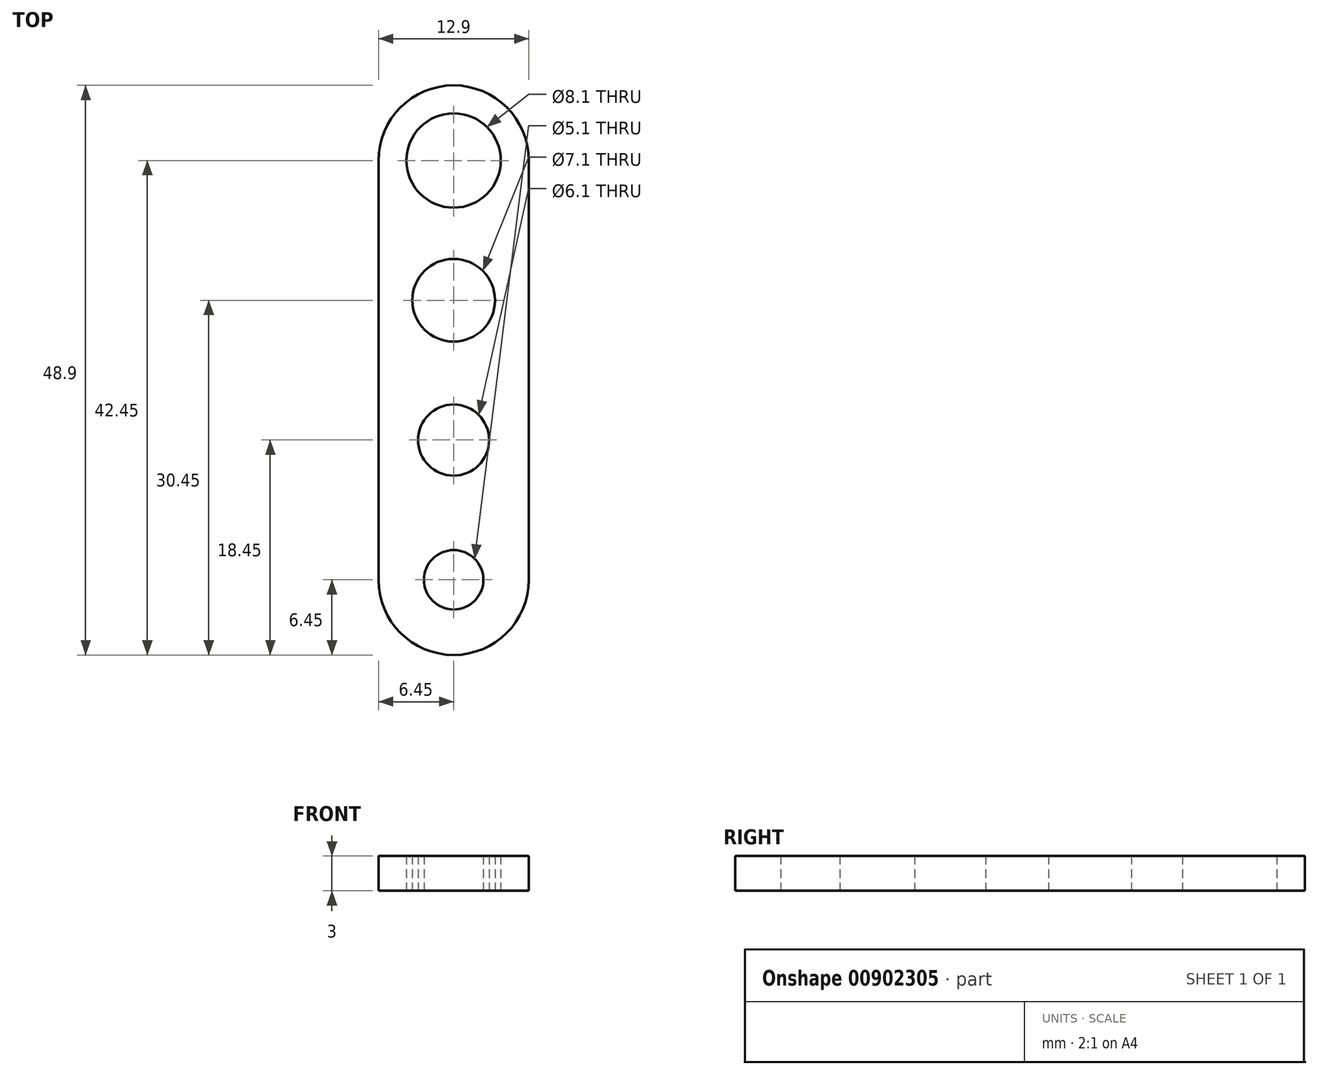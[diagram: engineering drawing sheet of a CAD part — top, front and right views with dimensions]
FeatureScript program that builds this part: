
annotation { "Feature Type Name" : "Feature", "Feature Type Description" : "" }
export const myFeature = defineFeature(function(context is Context, id is Id, definition is map)
    precondition{}
    {
        {
            var Q0;
            Q0=qCreatedBy(makeId("Top.planeOp"),FACE);
            var sketch = newSketch(context, id + "F0", { "sketchPlane" : qUnion([Q0])});
            skLineSegment(sketch, "E0.left", {"start": v(-6.45, -18) * mm, "end": v(-6.45, 18) * mm});
            skLineSegment(sketch, "E0.right", {"start": v(6.45, -18) * mm, "end": v(6.45, 18) * mm});
            skPoint(sketch, "E0.middle", {"position": v(0, 0) * mm});
            skArc(sketch, "E1", {"start": v(6.45, 18) * mm, "mid": v(0, 24.45) * mm, "end": v(-6.45, 18) * mm});
            skArc(sketch, "E2", {"start": v(-6.45, -18) * mm, "mid": v(0, -24.45) * mm, "end": v(6.45, -18) * mm});
            skCircle(sketch, "E3", {"center": v(0, 18) * mm, "radius": 4.05 * mm});
            skCircle(sketch, "E4", {"center": v(0, -18) * mm, "radius": 2.55 * mm});
            skCircle(sketch, "E5", {"center": v(0, 6) * mm, "radius": 3.55 * mm});
            skCircle(sketch, "E6", {"center": v(0, -6) * mm, "radius": 3.05 * mm});
            skSolve(sketch);
        }
        {
            var Q0;
            Q0 = qSketchRegion(id + "F0", true);
            extrude(context, id + "F1", {"entities" : qUnion([Q0]), "depth" : 3 * mm, "offsetDistance" : 25 * mm});
        }
    });
